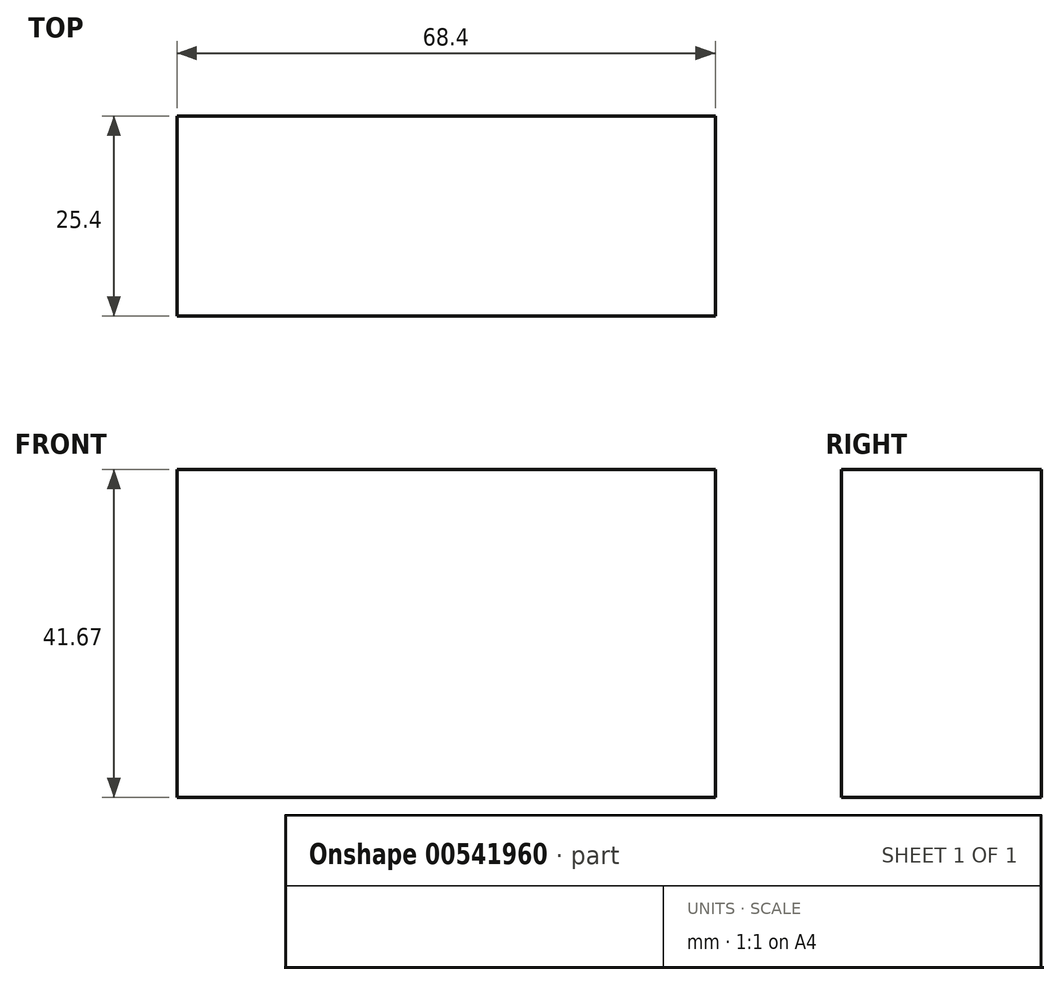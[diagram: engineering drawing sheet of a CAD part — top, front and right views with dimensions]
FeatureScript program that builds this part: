
annotation { "Feature Type Name" : "Feature", "Feature Type Description" : "" }
export const myFeature = defineFeature(function(context is Context, id is Id, definition is map)
    precondition{}
    {
        {
            var Q0;
            Q0=qCreatedBy(makeId("Front.planeOp"),FACE);
            var sketch = newSketch(context, id + "F0", { "sketchPlane" : qUnion([Q0])});
            skLineSegment(sketch, "E0.bottom", {"start": v(-99.37, 29.87) * mm, "end": v(-30.97, 29.87) * mm});
            skLineSegment(sketch, "E0.top", {"start": v(-99.37, -11.8) * mm, "end": v(-30.97, -11.8) * mm});
            skLineSegment(sketch, "E0.left", {"start": v(-99.37, 29.87) * mm, "end": v(-99.37, -11.8) * mm});
            skLineSegment(sketch, "E0.right", {"start": v(-30.97, 29.87) * mm, "end": v(-30.97, -11.8) * mm});
            skSolve(sketch);
        }
        {
            var Q0;
            Q0 = qSketchRegion(id + "F0", true);
            extrude(context, id + "F1", {"entities" : qUnion([Q0]), "depth" : 25.4 * mm, "offsetDistance" : 25.4 * mm});
        }
    });
